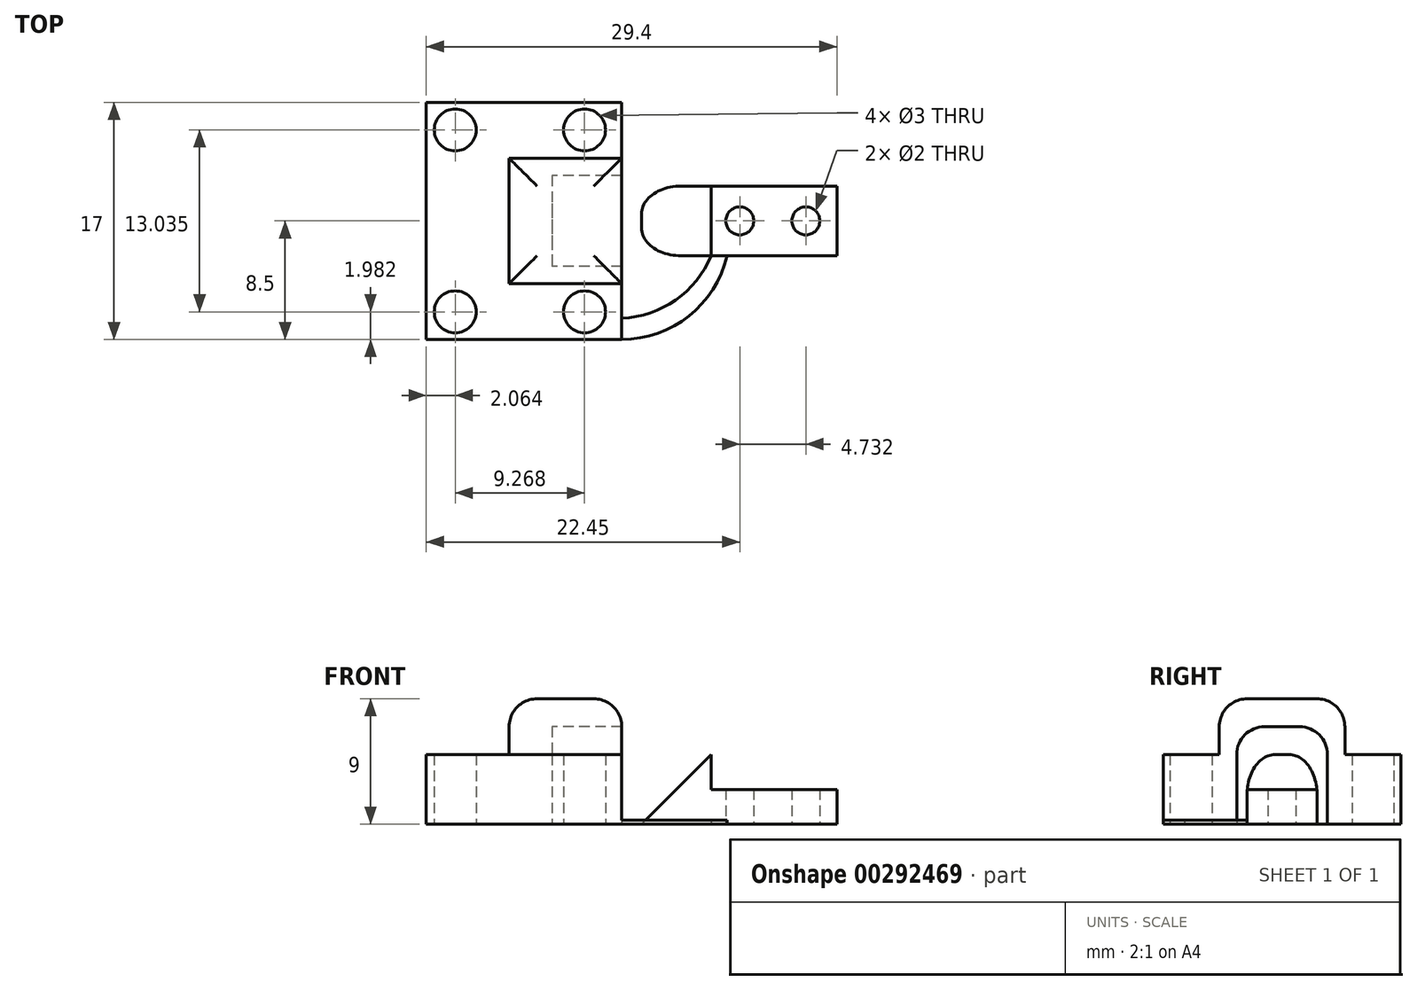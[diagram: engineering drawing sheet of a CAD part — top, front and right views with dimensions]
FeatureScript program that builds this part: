
annotation { "Feature Type Name" : "Feature", "Feature Type Description" : "" }
export const myFeature = defineFeature(function(context is Context, id is Id, definition is map)
    precondition{}
    {
        {
            var Q0;
            Q0=qCreatedBy(makeId("Top.planeOp"),FACE);
            var sketch = newSketch(context, id + "F0", { "sketchPlane" : qUnion([Q0])});
            skLineSegment(sketch, "E0.bottom", {"start": v(-2.69, 2.5) * mm, "end": v(11.31, 2.5) * mm});
            skLineSegment(sketch, "E0.top", {"start": v(-2.69, -2.5) * mm, "end": v(11.31, -2.5) * mm});
            skLineSegment(sketch, "E0.left", {"start": v(-2.69, 2.5) * mm, "end": v(-2.69, -2.5) * mm});
            skLineSegment(sketch, "E0.right", {"start": v(11.31, 2.5) * mm, "end": v(11.31, -2.5) * mm});
            skLineSegment(sketch, "E1", {"start": v(2.31, 2.5) * mm, "end": v(2.31, -2.5) * mm});
            skLineSegment(sketch, "E2.bottom", {"start": v(-18.1, 8.5) * mm, "end": v(-4.1, 8.5) * mm});
            skLineSegment(sketch, "E2.top", {"start": v(-18.1, -8.5) * mm, "end": v(-4.1, -8.5) * mm});
            skLineSegment(sketch, "E2.left", {"start": v(-18.1, 8.5) * mm, "end": v(-18.1, -8.5) * mm});
            skLineSegment(sketch, "E2.right", {"start": v(-4.1, 8.5) * mm, "end": v(-4.1, -8.5) * mm});
            skLineSegment(sketch, "E3.bottom", {"start": v(-4.1, 3.25) * mm, "end": v(-9.1, 3.25) * mm});
            skLineSegment(sketch, "E3.top", {"start": v(-4.1, -3.25) * mm, "end": v(-9.1, -3.25) * mm});
            skLineSegment(sketch, "E3.left", {"start": v(-4.1, 3.25) * mm, "end": v(-4.1, -3.25) * mm});
            skLineSegment(sketch, "E3.right", {"start": v(-9.1, 3.25) * mm, "end": v(-9.1, -3.25) * mm});
            skCircle(sketch, "E4", {"center": v(-16.03, 6.52) * mm, "radius": 1.5 * mm});
            skCircle(sketch, "E5", {"center": v(-6.76, 6.52) * mm, "radius": 1.5 * mm});
            skCircle(sketch, "E6.MirrorC", {"center": v(-16.03, -6.52) * mm, "radius": 1.5 * mm});
            skCircle(sketch, "E7.MirrorC", {"center": v(-6.76, -6.52) * mm, "radius": 1.5 * mm});
            skLineSegment(sketch, "E8", {"start": v(-4.1, 4.5) * mm, "end": v(-18.1, 4.5) * mm});
            skLineSegment(sketch, "E9.MirrorCS", {"start": v(-4.1, -4.5) * mm, "end": v(-18.1, -4.5) * mm});
            skCircle(sketch, "E10", {"center": v(4.36, 0) * mm, "radius": 1 * mm});
            skCircle(sketch, "E11", {"center": v(9.1, 0) * mm, "radius": 1 * mm});
            skLineSegment(sketch, "E12", {"start": v(-12.16, 4.5) * mm, "end": v(-12.16, -4.5) * mm});
            skArc(sketch, "E13", {"start": v(-4.1, -6.98) * mm, "mid": v(-0.24, -5.67) * mm, "end": v(2.31, -2.5) * mm});
            skArc(sketch, "E14", {"start": v(-4.1, -8.5) * mm, "mid": v(0.73, -6.82) * mm, "end": v(3.45, -2.5) * mm});
            skSolve(sketch);
        }
        {
            var Q0;
            Q0=makeQuery(id+"F0.imprint","IMPRINT",FACE,{"disambiguationData":[TD([[makeQuery(id+"F0.imprint","IMPRINT",EDGE,{"derivedFrom":sQuery(id+"F0.wireOp",EDGE,"E3.bottom")}),1.0]])]});
            var Q1;
            {var subQ1=sQuery(id+"F0.wireOp",EDGE,"E3.bottom");Q1=makeQuery(id+"F0.imprint","IMPRINT",FACE,{"disambiguationData":[TD([[makeQuery(id+"F0.imprint","IMPRINT",EDGE,{"derivedFrom":subQ1}),-1.0]])]});}
            extrude(context, id + "F1", {"entities" : qUnion([Q0, Q1]), "depth" : 9 * mm});
        }
        {
            var Q0;
            {var subQ0=sQuery(id+"F0.wireOp",EDGE,"E0.left");Q0=makeQuery(id+"F0.imprint","IMPRINT",FACE,{"disambiguationData":[TD([[makeQuery(id+"F0.imprint","IMPRINT",EDGE,{"derivedFrom":subQ0}),1.0]])]});}
            var Q1;
            {var subQ5=sQuery(id+"F0.wireOp",EDGE,"E12");Q1=makeQuery(id+"F0.imprint","IMPRINT",FACE,{"disambiguationData":[TD([[makeQuery(id+"F0.imprint","IMPRINT",EDGE,{"derivedFrom":subQ5}),-1.0]])]});}
            var Q2;
            {var subQ1=sQuery(id+"F0.wireOp",EDGE,"E2.bottom");Q2=makeQuery(id+"F0.imprint","IMPRINT",FACE,{"disambiguationData":[TD([[makeQuery(id+"F0.imprint","IMPRINT",EDGE,{"derivedFrom":subQ1}),-1.0]])]});}
            var Q3;
            {var subQ1=sQuery(id+"F0.wireOp",EDGE,"E2.top");Q3=makeQuery(id+"F0.imprint","IMPRINT",FACE,{"disambiguationData":[TD([[makeQuery(id+"F0.imprint","IMPRINT",EDGE,{"derivedFrom":subQ1}),1.0]])]});}
            extrude(context, id + "F2", {"entities" : qUnion([Q0, Q1, Q2, Q3]), "operationType" : NewBodyOperationType.ADD, "depth" : 5 * mm});
        }
        {
            var Q0;
            {var subQ0=sQuery(id+"F0.wireOp",EDGE,"E0.right");Q0=makeQuery(id+"F0.imprint","IMPRINT",FACE,{"disambiguationData":[TD([[makeQuery(id+"F0.imprint","IMPRINT",EDGE,{"derivedFrom":subQ0}),-1.0]])]});}
            extrude(context, id + "F3", {"entities" : qUnion([Q0]), "operationType" : NewBodyOperationType.ADD, "depth" : 2.5 * mm});
        }
        {
            var Q0;
            Q0=makeQuery(id+"F2.opExtrude","CAP_EDGE",EDGE,{"disambiguationData":[OSD([sQuery(id+"F0.wireOp",EDGE,"E0.left")])],"isStart":false});
            chamfer(context, id + "F4", {"entities" : qUnion([Q0]), "width" : 5 * mm, "tangentPropagation" : true});
        }
        {
            var Q0;
            Q0=makeQuery(id+"F0.imprint","IMPRINT",FACE,{"disambiguationData":[TD([[makeQuery(id+"F0.imprint","IMPRINT",EDGE,{"derivedFrom":sQuery(id+"F0.wireOp",EDGE,"E3.bottom")}),1.0]])]});
            extrude(context, id + "F5", {"entities" : qUnion([Q0]), "operationType" : NewBodyOperationType.REMOVE, "depth" : 7 * mm});
        }
        {
            var Q0;
            Q0=makeQuery(id+"F1.opExtrude","CAP_EDGE",EDGE,{"disambiguationData":[OSD([sQuery(id+"F0.wireOp",EDGE,"E9.MirrorCS")])],"isStart":false});
            var Q1;
            Q1=makeQuery(id+"F1.opExtrude","CAP_FACE",FACE,{"disambiguationData":[OSD([sQuery(id+"F0.wireOp",EDGE,"E2.right"),sQuery(id+"F0.wireOp",EDGE,"E3.left"),sQuery(id+"F0.wireOp",EDGE,"E8"),sQuery(id+"F0.wireOp",EDGE,"E9.MirrorCS"),sQuery(id+"F0.wireOp",EDGE,"E12")])],"isStart":false});
            var Q2;
            Q2=makeQuery(id+"F2.opExtrude","CAP_EDGE",EDGE,{"disambiguationData":[OSD([sQuery(id+"F0.wireOp",EDGE,"E9.MirrorCS")])],"isStart":false});
            var Q3;
            Q3=makeQuery(id+"F2.opExtrude","CAP_EDGE",EDGE,{"disambiguationData":[OSD([sQuery(id+"F0.wireOp",EDGE,"E12")])],"isStart":false});
            var Q4;
            Q4=makeQuery(id+"F2.opExtrude","CAP_EDGE",EDGE,{"disambiguationData":[OSD([sQuery(id+"F0.wireOp",EDGE,"E8")])],"isStart":false});
            fillet(context, id + "F6", {"entities" : qUnion([Q0, Q1, Q2, Q3, Q4]), "radius" : 2 * mm, "tangentPropagation" : true, "allowEdgeOverflow" : false});
        }
        {
            var Q0;
            {var subQ0=sQuery(id+"F0.wireOp",EDGE,"E13");Q0=makeQuery(id+"F0.imprint","IMPRINT",FACE,{"disambiguationData":[TD([[makeQuery(id+"F0.imprint","IMPRINT",EDGE,{"derivedFrom":subQ0}),-1.0]])]});}
            extrude(context, id + "F7", {"entities" : qUnion([Q0]), "operationType" : NewBodyOperationType.ADD, "depth" : .3 * mm});
        }
        {
            var Q0;
            {var subQ0=sQuery(id+"F0.wireOp",EDGE,"E0.top");Q0=makeQuery(id+"F4.opChamfer","BLEND_EDGE",EDGE,{"blendedFrom":[makeQuery(id+"F2.opExtrude","CAP_EDGE",EDGE,{"disambiguationData":[OSD([sQuery(id+"F0.wireOp",EDGE,"E0.left")])],"isStart":false}),makeQuery(id+"F3.boolean.opBoolean","MERGE",FACE,{"derivedFrom":[makeQuery(id+"F2.opExtrude","SWEPT_FACE",FACE,{"disambiguationData":[OSD([subQ0])]}),makeQuery(id+"F3.opExtrude","SWEPT_FACE",FACE,{"disambiguationData":[OSD([subQ0])]})]})],"blendedInto":[makeQuery(id+"F3.boolean.opBoolean","MERGE",FACE,{"derivedFrom":[makeQuery(id+"F2.opExtrude","SWEPT_FACE",FACE,{"disambiguationData":[OSD([subQ0])]}),makeQuery(id+"F3.opExtrude","SWEPT_FACE",FACE,{"disambiguationData":[OSD([subQ0])]})]})]});}
            var Q1;
            Q1=makeQuery(id+"F5.boolean.opBoolean","COPY",EDGE,{"derivedFrom":makeQuery(id+"F5.opExtrude","CAP_EDGE",EDGE,{"disambiguationData":[OSD([sQuery(id+"F0.wireOp",EDGE,"E3.bottom")])],"isStart":false})});
            var Q2;
            {var subQ0=sQuery(id+"F0.wireOp",EDGE,"E0.bottom");Q2=makeQuery(id+"F4.opChamfer","BLEND_EDGE",EDGE,{"blendedFrom":[makeQuery(id+"F2.opExtrude","CAP_EDGE",EDGE,{"disambiguationData":[OSD([sQuery(id+"F0.wireOp",EDGE,"E0.left")])],"isStart":false}),makeQuery(id+"F3.boolean.opBoolean","MERGE",FACE,{"derivedFrom":[makeQuery(id+"F2.opExtrude","SWEPT_FACE",FACE,{"disambiguationData":[OSD([subQ0])]}),makeQuery(id+"F3.opExtrude","SWEPT_FACE",FACE,{"disambiguationData":[OSD([subQ0])]})]})],"blendedInto":[makeQuery(id+"F3.boolean.opBoolean","MERGE",FACE,{"derivedFrom":[makeQuery(id+"F2.opExtrude","SWEPT_FACE",FACE,{"disambiguationData":[OSD([subQ0])]}),makeQuery(id+"F3.opExtrude","SWEPT_FACE",FACE,{"disambiguationData":[OSD([subQ0])]})]})]});}
            var Q3;
            Q3=makeQuery(id+"F5.boolean.opBoolean","COPY",EDGE,{"derivedFrom":makeQuery(id+"F5.opExtrude","CAP_EDGE",EDGE,{"disambiguationData":[OSD([sQuery(id+"F0.wireOp",EDGE,"E3.top")])],"isStart":false})});
            fillet(context, id + "F8", {"entities" : qUnion([Q0, Q1, Q2, Q3]), "radius" : 2 * mm, "tangentPropagation" : true, "allowEdgeOverflow" : false});
        }
    });
